# Revit family: EPN
name_source: partatom
category: Wyposażenie mechaniczne
revit_build: Autodesk Revit 2017 (Build: 20160225_1515(x64)
units: mm (PartAtom-declared; Revit-internal decimal feet)

## family parameters
Oparty na płaszczyźnie roboczej = Nie
Punkt obliczania pomieszczeń = Nie
Tnij formami wycięć po wczytaniu = Nie
Typ części = Normalny
Współdzielony = Nie
Wymiar okrągłego złącza = Użyj średnicy
Zawsze pionowo = Tak

## types (7) — shared parameters
Air_flow = 0.0 m³/h
D1 = 160 mm  [stored 0.524934 ft]
D2 = 140 mm  [stored 0.459318 ft]
Date = 01.2019
Electrical_motor_diameter = 70 mm  [stored 0.229659 ft]
Electrical_motor_length_back = 220 mm  [stored 0.721785 ft]
Frequency = 50 Hz
Height = 400 mm  [stored 1.31234 ft]
Pressure = 0.0 Pa
Producent = Rosenberg
Protection_class = IP55
Radius_1 = 200 mm  [stored 0.656168 ft]
Radius_2 = 184 mm
URL = https://www.rosenberg.pl
Version = 1
Voltage = 400 V
Width = 367 mm  [stored 1.20407 ft]
max.Ambient_temperature = 60 °C

## per-type parameters (varying)
| type | Base_width_1 | Base_width_2 | Current | Model | Power | Weight |
| IE 3- 160 | 140 mm  [stored 0.459318 ft] | 242 mm  [stored 0.793963 ft] | 1 A | IE 3 -160 | 0 kW | 11.00 kg |
| IE 3 - 225 | 190 mm | 329 mm  [stored 1.0794 ft] | 2 A | IE 3 - 225 | 1 kW | 0.00 kg |
| IE 3 - 200 | 190 mm | 329 mm  [stored 1.0794 ft] | 2 A | IE 3 - 225 | 1 kW | 0.00 kg |
| IE 3 - 250 | 190 mm | 329 mm  [stored 1.0794 ft] | 2 A | IE 3 - 225 | 1 kW | 0.00 kg |
| IE 3 - 280 | 190 mm | 329 mm  [stored 1.0794 ft] | 2 A | IE 3 - 225 | 1 kW | 0.00 kg |
| IE 3 - 315 | 190 mm | 329 mm  [stored 1.0794 ft] | 2 A | IE 3 - 225 | 1 kW | 0.00 kg |
| IE 3 - 355 | 190 mm | 329 mm  [stored 1.0794 ft] | 2 A | IE 3 - 225 | 1 kW | 0.00 kg |

note: [stored X ft] marks values corroborated as IEEE doubles in the binary element streams (Revit-internal decimal feet)
